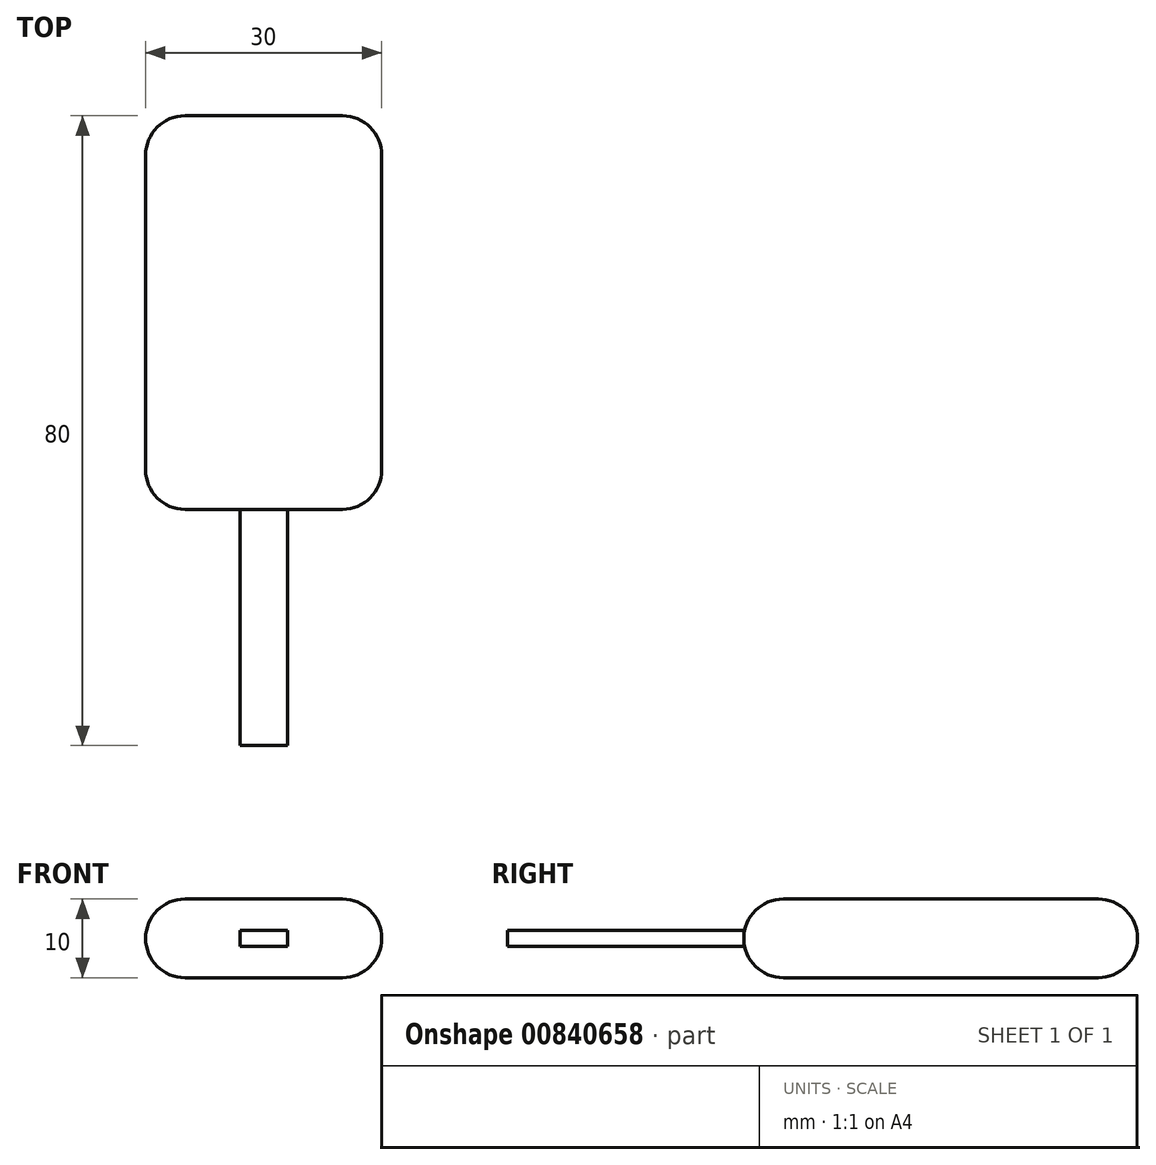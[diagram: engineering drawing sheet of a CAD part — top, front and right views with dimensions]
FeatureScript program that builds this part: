
annotation { "Feature Type Name" : "Feature", "Feature Type Description" : "" }
export const myFeature = defineFeature(function(context is Context, id is Id, definition is map)
    precondition{}
    {
        {
            var Q0;
            Q0=qCreatedBy(makeId("Top.planeOp"),FACE);
            var sketch = newSketch(context, id + "F0", { "sketchPlane" : qUnion([Q0])});
            skLineSegment(sketch, "E0.bottom", {"start": v(-15, 25) * mm, "end": v(15, 25) * mm});
            skLineSegment(sketch, "E0.top", {"start": v(-15, -25) * mm, "end": v(15, -25) * mm});
            skLineSegment(sketch, "E0.left", {"start": v(-15, 25) * mm, "end": v(-15, -25) * mm});
            skLineSegment(sketch, "E0.right", {"start": v(15, 25) * mm, "end": v(15, -25) * mm});
            skPoint(sketch, "E0.middle", {"position": v(0, 0) * mm});
            skSolve(sketch);
        }
        {
            var Q0;
            Q0 = qSketchRegion(id + "F0", true);
            extrude(context, id + "F1", {"entities" : qUnion([Q0]), "endBound" : BoundingType.SYMMETRIC, "depth" : 10 * mm, "offsetDistance" : 25 * mm});
        }
        {
            var Q0;
            Q0=makeQuery(id+"F1.opExtrude","SWEPT_FACE",FACE,{"disambiguationData":[OSD([sQuery(id+"F0.wireOp",EDGE,"E0.bottom")])]});
            var Q1;
            Q1=makeQuery(id+"F1.opExtrude","SWEPT_FACE",FACE,{"disambiguationData":[OSD([sQuery(id+"F0.wireOp",EDGE,"E0.left")])]});
            var Q2;
            Q2=makeQuery(id+"F1.opExtrude","SWEPT_FACE",FACE,{"disambiguationData":[OSD([sQuery(id+"F0.wireOp",EDGE,"E0.right")])]});
            fillet(context, id + "F2", {"entities" : qUnion([Q0, Q1, Q2]), "radius" : 5 * mm, "tangentPropagation" : true, "allowEdgeOverflow" : false});
        }
        {
            var Q0;
            Q0=makeQuery(id+"F1.opExtrude","SWEPT_FACE",FACE,{"disambiguationData":[OSD([sQuery(id+"F0.wireOp",EDGE,"E0.top")])]});
            var sketch = newSketch(context, id + "F3", { "sketchPlane" : qUnion([Q0])});
            skLineSegment(sketch, "E1.bottom", {"start": v(3, -1) * mm, "end": v(-3, -1) * mm});
            skLineSegment(sketch, "E1.top", {"start": v(3, 1) * mm, "end": v(-3, 1) * mm});
            skLineSegment(sketch, "E1.left", {"start": v(3, -1) * mm, "end": v(3, 1) * mm});
            skLineSegment(sketch, "E1.right", {"start": v(-3, -1) * mm, "end": v(-3, 1) * mm});
            skPoint(sketch, "E1.middle", {"position": v(0, 0) * mm});
            skSolve(sketch);
        }
        {
            var Q0;
            Q0 = qSketchRegion(id + "F3", true);
            extrude(context, id + "F4", {"entities" : qUnion([Q0]), "depth" : 30 * mm, "offsetDistance" : 25 * mm});
        }
        {
            var Q0;
            Q0=makeQuery(id+"F1.opExtrude","CAP_FACE",FACE,{"disambiguationData":[OSD([sQuery(id+"F0.wireOp",EDGE,"E0.bottom"),sQuery(id+"F0.wireOp",EDGE,"E0.top"),sQuery(id+"F0.wireOp",EDGE,"E0.left"),sQuery(id+"F0.wireOp",EDGE,"E0.right")])],"isStart":false});
            var Q1;
            Q1=makeQuery(id+"F1.opExtrude","CAP_FACE",FACE,{"disambiguationData":[OSD([sQuery(id+"F0.wireOp",EDGE,"E0.bottom"),sQuery(id+"F0.wireOp",EDGE,"E0.top"),sQuery(id+"F0.wireOp",EDGE,"E0.left"),sQuery(id+"F0.wireOp",EDGE,"E0.right")])],"isStart":true});
            fillet(context, id + "F5", {"entities" : qUnion([Q0, Q1]), "radius" : 5 * mm, "tangentPropagation" : true, "allowEdgeOverflow" : false});
        }
    });
